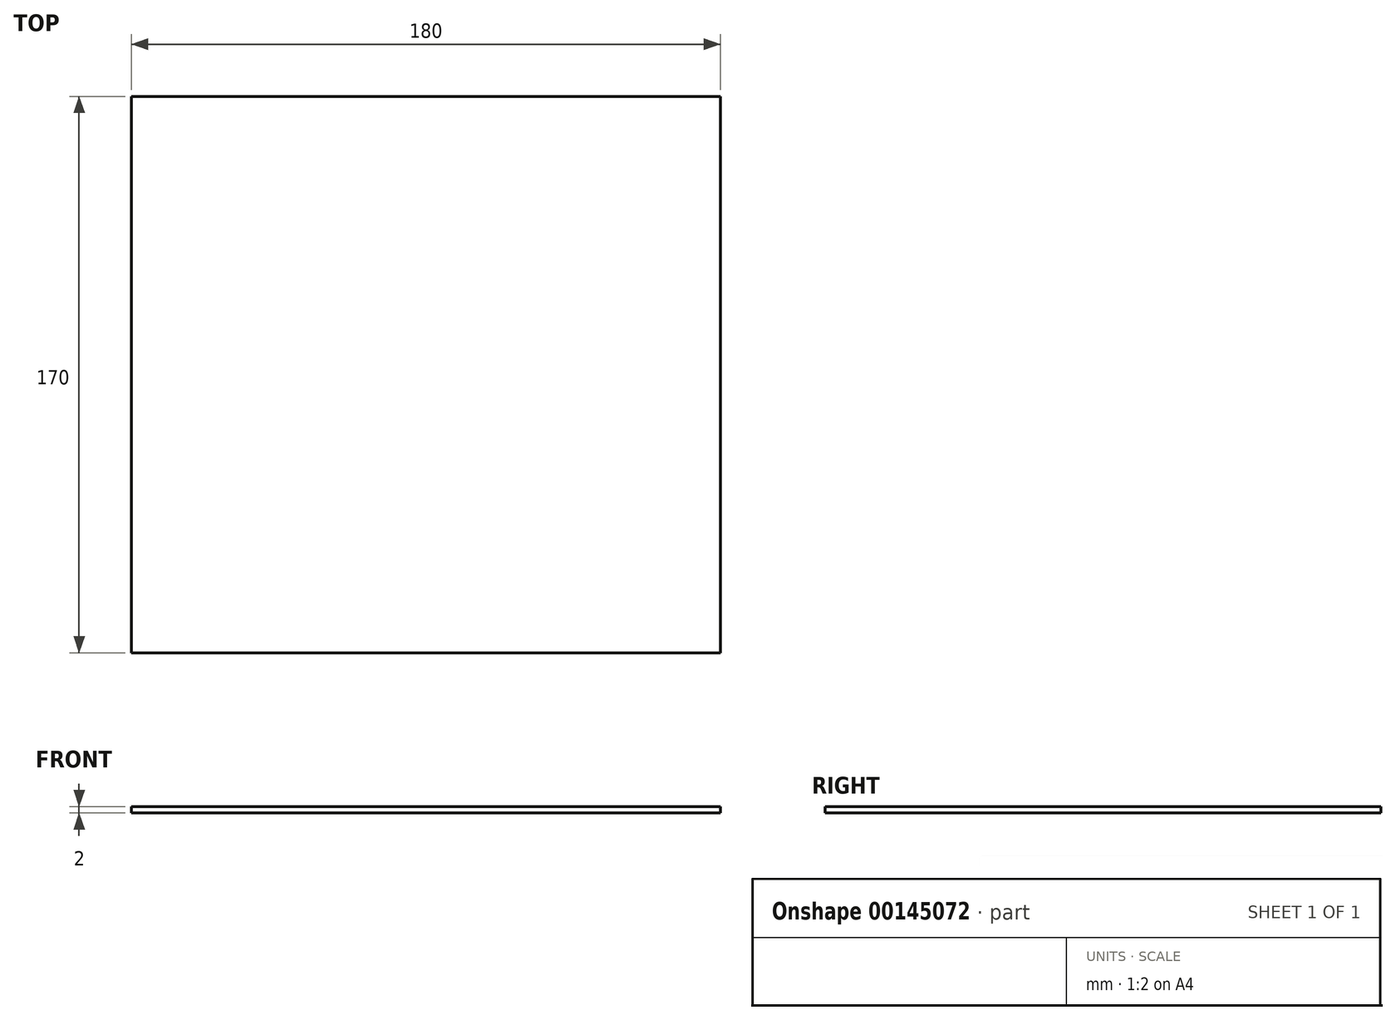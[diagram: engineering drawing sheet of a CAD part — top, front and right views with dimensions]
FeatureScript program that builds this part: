
annotation { "Feature Type Name" : "Feature", "Feature Type Description" : "" }
export const myFeature = defineFeature(function(context is Context, id is Id, definition is map)
    precondition{}
    {
        {
            var Q0;
            Q0=qCreatedBy(makeId("Top.planeOp"),FACE);
            var sketch = newSketch(context, id + "F0", { "sketchPlane" : qUnion([Q0])});
            skLineSegment(sketch, "E0.bottom", {"start": v(0, 0) * mm, "end": v(180, 0) * mm});
            skLineSegment(sketch, "E0.top", {"start": v(0, 170) * mm, "end": v(180, 170) * mm});
            skLineSegment(sketch, "E0.left", {"start": v(0, 0) * mm, "end": v(0, 170) * mm});
            skLineSegment(sketch, "E0.right", {"start": v(180, 0) * mm, "end": v(180, 170) * mm});
            skSolve(sketch);
        }
        {
            var Q0;
            Q0 = qSketchRegion(id + "F0", true);
            extrude(context, id + "F1", {"entities" : qUnion([Q0]), "depth" : 2 * mm});
        }
    });
